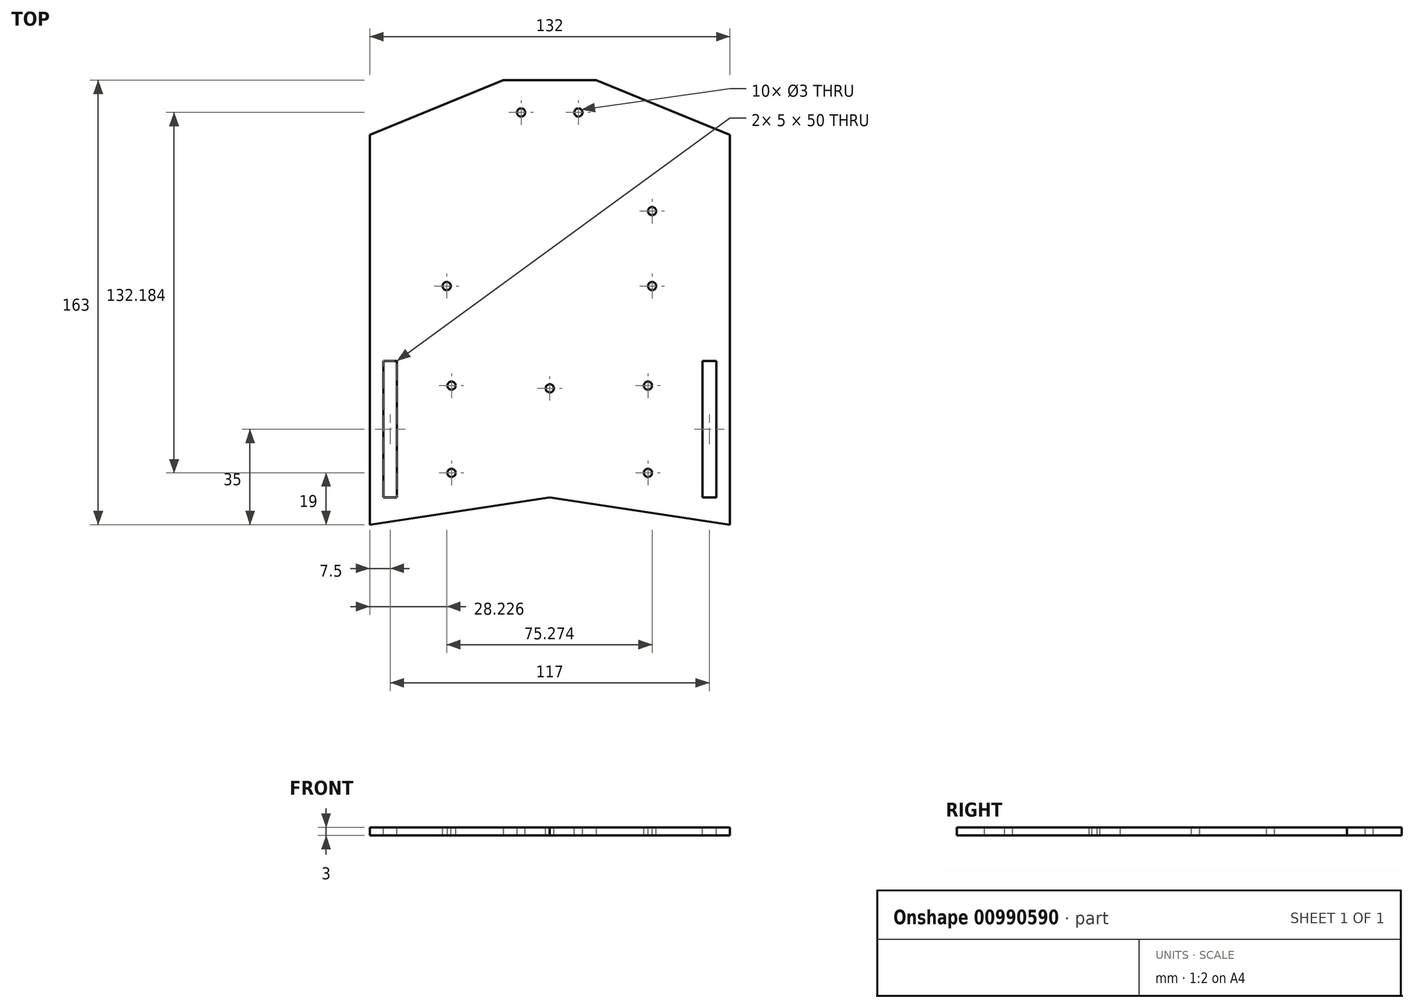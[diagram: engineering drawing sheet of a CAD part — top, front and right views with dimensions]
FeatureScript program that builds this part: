
annotation { "Feature Type Name" : "Feature", "Feature Type Description" : "" }
export const myFeature = defineFeature(function(context is Context, id is Id, definition is map)
    precondition{}
    {
        {
            var Q0;
            Q0=qCreatedBy(makeId("Top.planeOp"),FACE);
            var sketch = newSketch(context, id + "F0", { "sketchPlane" : qUnion([Q0])});
            skLineSegment(sketch, "E0.bottom", {"start": v(0, 0) * mm, "end": v(66, 0) * mm});
            skLineSegment(sketch, "E0.top", {"start": v(0, 163) * mm, "end": v(66, 163) * mm});
            skLineSegment(sketch, "E0.left", {"start": v(0, 0) * mm, "end": v(0, 163) * mm});
            skLineSegment(sketch, "E0.right", {"start": v(66, 0) * mm, "end": v(66, 163) * mm});
            skLineSegment(sketch, "E1", {"start": v(0, 0) * mm, "end": v(0, 10) * mm});
            skLineSegment(sketch, "E2", {"start": v(66, 0) * mm, "end": v(0, 10) * mm});
            skLineSegment(sketch, "E3", {"start": v(0, 163) * mm, "end": v(17, 163) * mm});
            skLineSegment(sketch, "E4", {"start": v(17, 163) * mm, "end": v(66, 143) * mm});
            skSolve(sketch);
        }
        {
            var Q0;
            {var subQ0=sQuery(id+"F0.wireOp",EDGE,"E2");Q0=makeQuery(id+"F0.imprint","IMPRINT",FACE,{"disambiguationData":[TD([[makeQuery(id+"F0.imprint","IMPRINT",EDGE,{"derivedFrom":subQ0}),-1.0]])]});}
            extrude(context, id + "F1", {"entities" : qUnion([Q0]), "depth" : 3 * mm, "offsetDistance" : 25 * mm});
        }
        {
            var Q0;
            Q0=makeQuery(id+"F1.opExtrude","CAP_FACE",FACE,{"disambiguationData":[OSD([sQuery(id+"F0.wireOp",EDGE,"E0.top"),sQuery(id+"F0.wireOp",EDGE,"E0.left"),sQuery(id+"F0.wireOp",EDGE,"E0.right"),sQuery(id+"F0.wireOp",EDGE,"E2"),sQuery(id+"F0.wireOp",EDGE,"E4")])],"isStart":false});
            var sketch = newSketch(context, id + "F2", { "sketchPlane" : qUnion([Q0])});
            skLineSegment(sketch, "E5", {"start": v(66, 0) * mm, "end": v(66, 10) * mm});
            skLineSegment(sketch, "E6.bottom", {"start": v(61, 10) * mm, "end": v(56, 10) * mm});
            skLineSegment(sketch, "E6.top", {"start": v(61, 60) * mm, "end": v(56, 60) * mm});
            skLineSegment(sketch, "E6.left", {"start": v(61, 10) * mm, "end": v(61, 60) * mm});
            skLineSegment(sketch, "E6.right", {"start": v(56, 10) * mm, "end": v(56, 60) * mm});
            skSolve(sketch);
        }
        {
            var Q0;
            Q0=makeQuery(id+"F2.imprint","IMPRINT",FACE,{"disambiguationData":[TD([[makeQuery(id+"F2.imprint","IMPRINT",EDGE,{"derivedFrom":sQuery(id+"F2.wireOp",EDGE,"E6.bottom")}),-1.0]])]});
            extrude(context, id + "F3", {"entities" : qUnion([Q0]), "operationType" : NewBodyOperationType.REMOVE, "oppositeDirection" : true, "depth" : 3 * mm, "offsetDistance" : 25 * mm});
        }
        {
            var Q0;
            Q0=makeQuery(id+"F1.opExtrude","CAP_FACE",FACE,{"disambiguationData":[OSD([sQuery(id+"F0.wireOp",EDGE,"E0.top"),sQuery(id+"F0.wireOp",EDGE,"E0.left"),sQuery(id+"F0.wireOp",EDGE,"E0.right"),sQuery(id+"F0.wireOp",EDGE,"E2"),sQuery(id+"F0.wireOp",EDGE,"E4")])],"isStart":false});
            var sketch = newSketch(context, id + "F4", { "sketchPlane" : qUnion([Q0])});
            skLineSegment(sketch, "E7", {"start": v(56, 60) * mm, "end": v(36, 60) * mm});
            skLineSegment(sketch, "E8", {"start": v(36, 10) * mm, "end": v(36, 19) * mm});
            skLineSegment(sketch, "E9", {"start": v(36, 60) * mm, "end": v(36, 51) * mm});
            skPoint(sketch, "E10", {"position": v(36, 51) * mm});
            skPoint(sketch, "E11", {"position": v(36, 19) * mm});
            skSolve(sketch);
        }
        {
            var Q0;
            Q0=sQuery(id+"F4.wireOp",VERTEX,"E11");
            var Q1;
            Q1=sQuery(id+"F4.wireOp",VERTEX,"E10");
            var Q2;
            Q2=makeQuery(id+"F1.opExtrude","SWEPT_BODY",BODY,{"disambiguationData":[OSD([sQuery(id+"F0.wireOp",EDGE,"E0.top"),sQuery(id+"F0.wireOp",EDGE,"E0.left"),sQuery(id+"F0.wireOp",EDGE,"E0.right"),sQuery(id+"F0.wireOp",EDGE,"E2"),sQuery(id+"F0.wireOp",EDGE,"E4")])]});
            hole(context, id + "F5", {"style" : HoleStyle.SIMPLE, "endStyle" : HoleEndStyle.THROUGH, "holeDiameter" : 3 * mm, "majorDiameter" : 5 * mm, "isTappedThrough" : true, "tappedDepth" : 12 * mm, "tapClearance" : 3, "locations" : qUnion([Q0, Q1]), "scope" : qUnion([Q2])});
        }
        {
            var Q0;
            Q0=makeQuery(id+"F1.opExtrude","SWEPT_BODY",BODY,{"disambiguationData":[OSD([sQuery(id+"F0.wireOp",EDGE,"E0.top"),sQuery(id+"F0.wireOp",EDGE,"E0.left"),sQuery(id+"F0.wireOp",EDGE,"E0.right"),sQuery(id+"F0.wireOp",EDGE,"E2"),sQuery(id+"F0.wireOp",EDGE,"E4")])]});
            var Q1;
            Q1=qCreatedBy(makeId("Right.planeOp"),FACE);
            mirror(context, id + "F6", {"operationType" : NewBodyOperationType.ADD, "entities" : qUnion([Q0]), "mirrorPlane" : qUnion([Q1])});
        }
        {
            var Q0;
            {var subQ0=makeQuery(id+"F1.opExtrude","CAP_FACE",FACE,{"disambiguationData":[OSD([sQuery(id+"F0.wireOp",EDGE,"E0.top"),sQuery(id+"F0.wireOp",EDGE,"E0.left"),sQuery(id+"F0.wireOp",EDGE,"E0.right"),sQuery(id+"F0.wireOp",EDGE,"E2"),sQuery(id+"F0.wireOp",EDGE,"E4")])],"isStart":false});Q0=makeQuery(id+"F6.boolean.opBoolean","MERGE",FACE,{"derivedFrom":[subQ0,makeQuery(id+"F6.opPattern","COPY",FACE,{"derivedFrom":subQ0,"instanceName":"1"})]});}
            var sketch = newSketch(context, id + "F7", { "sketchPlane" : qUnion([Q0])});
            skLineSegment(sketch, "E12", {"start": v(56, 10) * mm, "end": v(21, 10) * mm});
            skLineSegment(sketch, "E13", {"start": v(21, 10) * mm, "end": v(11, 10) * mm});
            skLineSegment(sketch, "E14", {"start": v(11, 10) * mm, "end": v(-11, 10) * mm});
            skLineSegment(sketch, "E15", {"start": v(11, 10) * mm, "end": v(11, 50) * mm});
            skPoint(sketch, "E16", {"position": v(0, 50) * mm});
            skSolve(sketch);
        }
        {
            var Q0;
            Q0=sQuery(id+"F7.wireOp",VERTEX,"E16");
            var Q1;
            Q1=makeQuery(id+"F1.opExtrude","SWEPT_BODY",BODY,{"disambiguationData":[OSD([sQuery(id+"F0.wireOp",EDGE,"E0.top"),sQuery(id+"F0.wireOp",EDGE,"E0.left"),sQuery(id+"F0.wireOp",EDGE,"E0.right"),sQuery(id+"F0.wireOp",EDGE,"E2"),sQuery(id+"F0.wireOp",EDGE,"E4")])]});
            hole(context, id + "F8", {"style" : HoleStyle.SIMPLE, "endStyle" : HoleEndStyle.THROUGH, "holeDiameter" : 3 * mm, "majorDiameter" : 5 * mm, "isTappedThrough" : true, "tappedDepth" : 12 * mm, "tapClearance" : 3, "locations" : qUnion([Q0]), "scope" : qUnion([Q1])});
        }
        {
            var Q0;
            {var subQ0=makeQuery(id+"F1.opExtrude","CAP_FACE",FACE,{"disambiguationData":[OSD([sQuery(id+"F0.wireOp",EDGE,"E0.top"),sQuery(id+"F0.wireOp",EDGE,"E0.left"),sQuery(id+"F0.wireOp",EDGE,"E0.right"),sQuery(id+"F0.wireOp",EDGE,"E2"),sQuery(id+"F0.wireOp",EDGE,"E4")])],"isStart":false});Q0=makeQuery(id+"F6.boolean.opBoolean","MERGE",FACE,{"derivedFrom":[subQ0,makeQuery(id+"F6.opPattern","COPY",FACE,{"derivedFrom":subQ0,"instanceName":"1"})]});}
            var sketch = newSketch(context, id + "F9", { "sketchPlane" : qUnion([Q0])});
            skLineSegment(sketch, "E17", {"start": v(42.5, 60) * mm, "end": v(42.5, 70) * mm});
            skLineSegment(sketch, "E18", {"start": v(42.5, 70) * mm, "end": v(42.5, 105) * mm});
            skLineSegment(sketch, "E19", {"start": v(42.5, 70) * mm, "end": v(-42.5, 70) * mm});
            skLineSegment(sketch, "E20", {"start": v(42.5, 70) * mm, "end": v(37.5, 70) * mm});
            skLineSegment(sketch, "E21", {"start": v(-42.5, 70) * mm, "end": v(-37.5, 70) * mm});
            skPoint(sketch, "E22", {"position": v(37.5, 87.5) * mm});
            skPoint(sketch, "E23", {"position": v(-37.77, 87.5) * mm});
            skSolve(sketch);
        }
        {
            var Q0;
            Q0=sQuery(id+"F9.wireOp",VERTEX,"E23");
            var Q1;
            Q1=sQuery(id+"F9.wireOp",VERTEX,"E22");
            var Q2;
            Q2=makeQuery(id+"F1.opExtrude","SWEPT_BODY",BODY,{"disambiguationData":[OSD([sQuery(id+"F0.wireOp",EDGE,"E0.top"),sQuery(id+"F0.wireOp",EDGE,"E0.left"),sQuery(id+"F0.wireOp",EDGE,"E0.right"),sQuery(id+"F0.wireOp",EDGE,"E2"),sQuery(id+"F0.wireOp",EDGE,"E4")])]});
            hole(context, id + "F10", {"style" : HoleStyle.SIMPLE, "endStyle" : HoleEndStyle.THROUGH, "holeDiameter" : 3 * mm, "majorDiameter" : 5 * mm, "isTappedThrough" : true, "tappedDepth" : 12 * mm, "tapClearance" : 3, "locations" : qUnion([Q0, Q1]), "scope" : qUnion([Q2])});
        }
        {
            var Q0;
            {var subQ0=makeQuery(id+"F1.opExtrude","CAP_FACE",FACE,{"disambiguationData":[OSD([sQuery(id+"F0.wireOp",EDGE,"E0.top"),sQuery(id+"F0.wireOp",EDGE,"E0.left"),sQuery(id+"F0.wireOp",EDGE,"E0.right"),sQuery(id+"F0.wireOp",EDGE,"E2"),sQuery(id+"F0.wireOp",EDGE,"E4")])],"isStart":false});Q0=makeQuery(id+"F6.boolean.opBoolean","MERGE",FACE,{"derivedFrom":[subQ0,makeQuery(id+"F6.opPattern","COPY",FACE,{"derivedFrom":subQ0,"instanceName":"1"})]});}
            var sketch = newSketch(context, id + "F11", { "sketchPlane" : qUnion([Q0])});
            skLineSegment(sketch, "E24", {"start": v(37.5, 87.5) * mm, "end": v(37.5, 97.5) * mm});
            skLineSegment(sketch, "E25.bottom", {"start": v(37.5, 97.5) * mm, "end": v(-27.5, 97.5) * mm});
            skLineSegment(sketch, "E25.top", {"start": v(37.5, 132.5) * mm, "end": v(-27.5, 132.5) * mm});
            skLineSegment(sketch, "E25.left", {"start": v(37.5, 97.5) * mm, "end": v(37.5, 132.5) * mm});
            skLineSegment(sketch, "E25.right", {"start": v(-27.5, 97.5) * mm, "end": v(-27.5, 132.5) * mm});
            skPoint(sketch, "E26", {"position": v(37.5, 115) * mm});
            skSolve(sketch);
        }
        {
            var Q0;
            Q0=sQuery(id+"F11.wireOp",VERTEX,"E26");
            var Q1;
            Q1=makeQuery(id+"F1.opExtrude","SWEPT_BODY",BODY,{"disambiguationData":[OSD([sQuery(id+"F0.wireOp",EDGE,"E0.top"),sQuery(id+"F0.wireOp",EDGE,"E0.left"),sQuery(id+"F0.wireOp",EDGE,"E0.right"),sQuery(id+"F0.wireOp",EDGE,"E2"),sQuery(id+"F0.wireOp",EDGE,"E4")])]});
            hole(context, id + "F12", {"style" : HoleStyle.SIMPLE, "endStyle" : HoleEndStyle.THROUGH, "holeDiameter" : 3 * mm, "majorDiameter" : 5 * mm, "isTappedThrough" : true, "tappedDepth" : 12 * mm, "tapClearance" : 3, "locations" : qUnion([Q0]), "scope" : qUnion([Q1])});
        }
        {
            var Q0;
            Q0=makeQuery(id+"F11.imprint","IMPRINT",FACE,{"disambiguationData":[TD([[makeQuery(id+"F11.imprint","IMPRINT",EDGE,{"derivedFrom":sQuery(id+"F11.wireOp",EDGE,"E25.bottom")}),1.0]])]});
            var sketch = newSketch(context, id + "F13", { "sketchPlane" : qUnion([Q0])});
            skPoint(sketch, "E27", {"position": v(-10.5, 151.18) * mm});
            skPoint(sketch, "E28", {"position": v(10.5, 151.18) * mm});
            skSolve(sketch);
        }
        {
            var Q0;
            Q0=sQuery(id+"F13.wireOp",VERTEX,"E27");
            var Q1;
            Q1=sQuery(id+"F13.wireOp",VERTEX,"E28");
            var Q2;
            Q2=makeQuery(id+"F1.opExtrude","SWEPT_BODY",BODY,{"disambiguationData":[OSD([sQuery(id+"F0.wireOp",EDGE,"E0.top"),sQuery(id+"F0.wireOp",EDGE,"E0.left"),sQuery(id+"F0.wireOp",EDGE,"E0.right"),sQuery(id+"F0.wireOp",EDGE,"E2"),sQuery(id+"F0.wireOp",EDGE,"E4")])]});
            hole(context, id + "F14", {"style" : HoleStyle.SIMPLE, "endStyle" : HoleEndStyle.THROUGH, "holeDiameter" : 3 * mm, "majorDiameter" : 5 * mm, "isTappedThrough" : true, "tappedDepth" : 12 * mm, "tapClearance" : 3, "locations" : qUnion([Q0, Q1]), "scope" : qUnion([Q2])});
        }
    });
